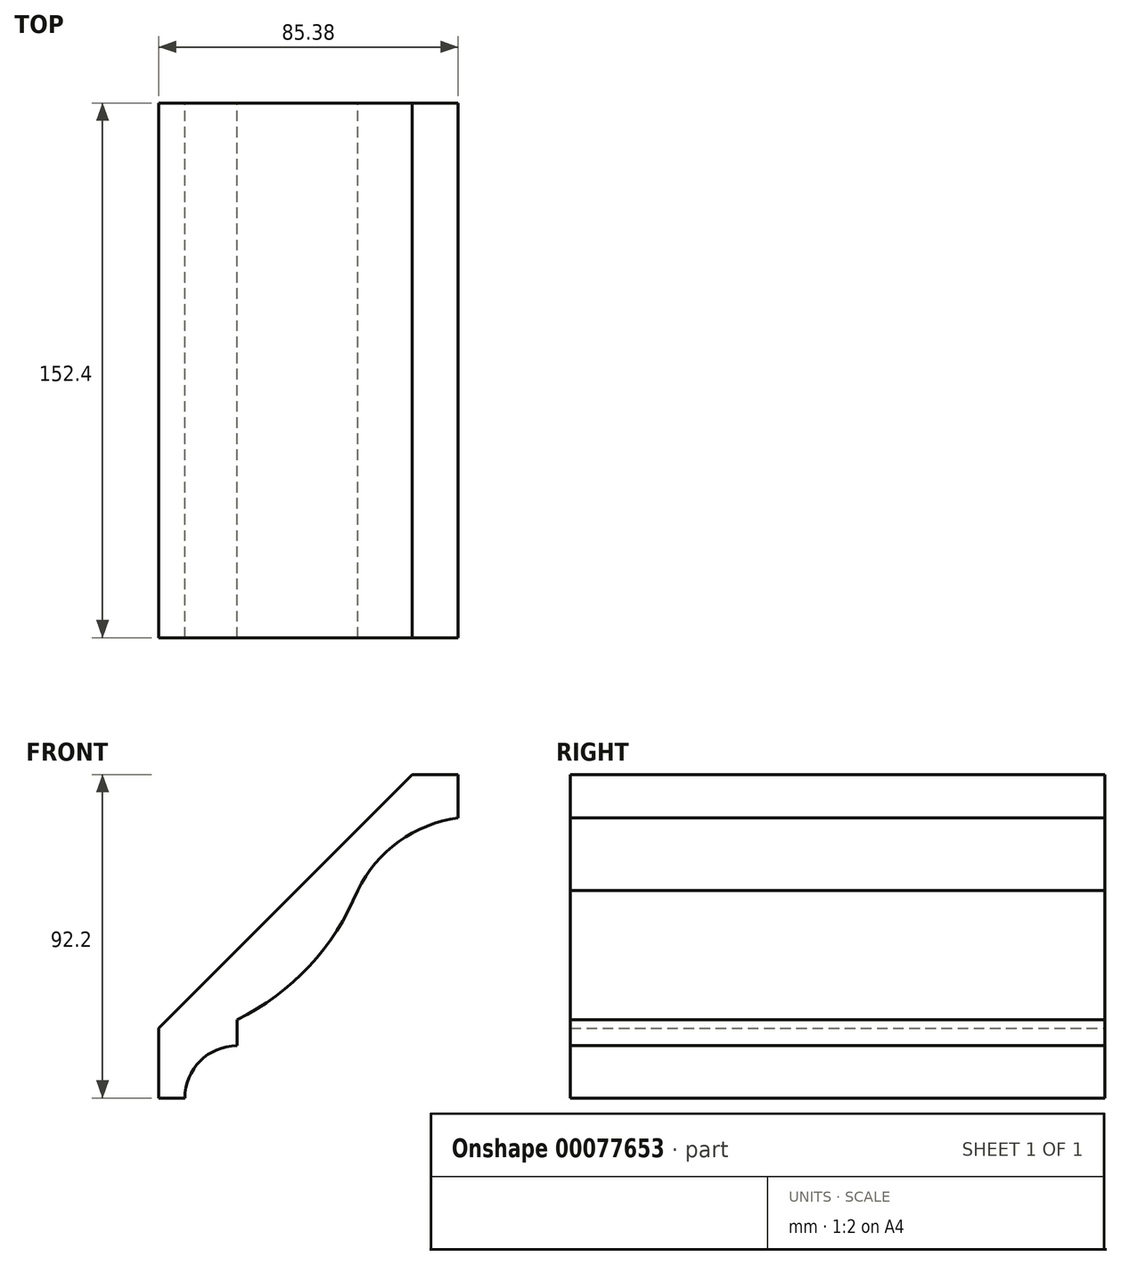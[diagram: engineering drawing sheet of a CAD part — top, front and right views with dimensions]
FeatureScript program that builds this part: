
annotation { "Feature Type Name" : "Feature", "Feature Type Description" : "" }
export const myFeature = defineFeature(function(context is Context, id is Id, definition is map)
    precondition{}
    {
        {
            var Q0;
            Q0=qCreatedBy(makeId("Front.planeOp"),FACE);
            var sketch = newSketch(context, id + "F0", { "sketchPlane" : qUnion([Q0])});
            skLineSegment(sketch, "E0", {"start": v(42.69, 46.1) * mm, "end": v(42.69, 33.7) * mm});
            skLineSegment(sketch, "E1", {"start": v(-42.69, -46.1) * mm, "end": v(-35.25, -46.1) * mm});
            skLineSegment(sketch, "E2", {"start": v(-20.37, -31.22) * mm, "end": v(-20.37, -23.79) * mm});
            skArc(sketch, "E3", {"start": v(-20.37, -31.22) * mm, "mid": v(-30.9, -35.58) * mm, "end": v(-35.25, -46.1) * mm});
            skLineSegment(sketch, "E4", {"start": v(-42.69, -46.1) * mm, "end": v(-42.69, -26.27) * mm});
            skLineSegment(sketch, "E5", {"start": v(-42.69, -26.27) * mm, "end": v(29.57, 46.1) * mm});
            skLineSegment(sketch, "E6", {"start": v(29.57, 46.1) * mm, "end": v(42.69, 46.1) * mm});
            skArc(sketch, "E7", {"start": v(42.69, 33.7) * mm, "mid": v(25.75, 26.98) * mm, "end": v(14, 13.04) * mm});
            skArc(sketch, "E8", {"start": v(-20.37, -23.79) * mm, "mid": v(0.2, -8.54) * mm, "end": v(14, 13.04) * mm});
            skSolve(sketch);
        }
        {
            var Q0;
            Q0=makeQuery(id+"F0.imprint","IMPRINT",FACE,{"disambiguationData":[TD([[makeQuery(id+"F0.imprint","IMPRINT",EDGE,{"derivedFrom":sQuery(id+"F0.wireOp",EDGE,"E0")}),-1.0]])]});
            extrude(context, id + "F1", {"entities" : qUnion([Q0]), "depth" : 152.4 * mm});
        }
    });
